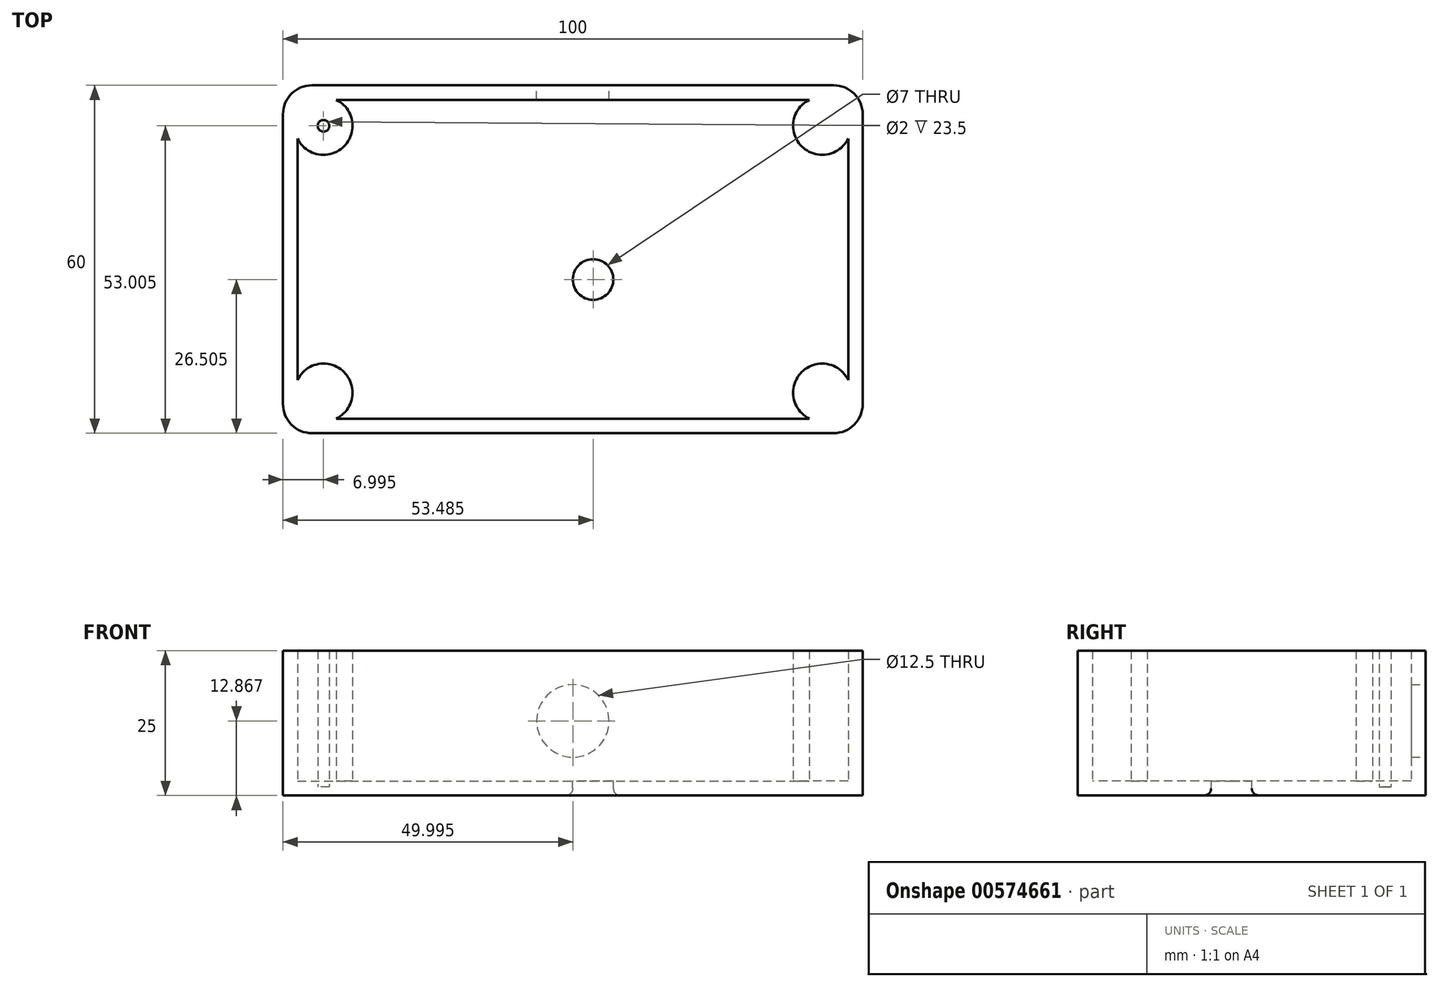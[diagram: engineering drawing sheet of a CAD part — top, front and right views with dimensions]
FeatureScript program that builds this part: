
annotation { "Feature Type Name" : "Feature", "Feature Type Description" : "" }
export const myFeature = defineFeature(function(context is Context, id is Id, definition is map)
    precondition{}
    {
        {
            var Q0;
            Q0=qCreatedBy(makeId("Top.planeOp"),FACE);
            var sketch = newSketch(context, id + "F0", { "sketchPlane" : qUnion([Q0])});
            skLineSegment(sketch, "E0.bottom", {"start": v(-26.94, 44.14) * mm, "end": v(73.06, 44.14) * mm});
            skLineSegment(sketch, "E0.top", {"start": v(-26.94, -15.86) * mm, "end": v(73.06, -15.86) * mm});
            skLineSegment(sketch, "E0.left", {"start": v(-26.94, 44.14) * mm, "end": v(-26.94, -15.86) * mm});
            skLineSegment(sketch, "E0.right", {"start": v(73.06, 44.14) * mm, "end": v(73.06, -15.86) * mm});
            skSolve(sketch);
        }
        {
            var Q0;
            Q0=makeQuery(id+"F0.imprint","IMPRINT",FACE,{"disambiguationData":[TD([[makeQuery(id+"F0.imprint","IMPRINT",EDGE,{"derivedFrom":sQuery(id+"F0.wireOp",EDGE,"E0.bottom")}),-1.0]])]});
            extrude(context, id + "F1", {"entities" : qUnion([Q0]), "depth" : 25 * mm, "offsetDistance" : 25 * mm});
        }
        {
            var Q0;
            Q0=makeQuery(id+"F1.opExtrude","CAP_FACE",FACE,{"disambiguationData":[OSD([sQuery(id+"F0.wireOp",EDGE,"E0.bottom"),sQuery(id+"F0.wireOp",EDGE,"E0.top"),sQuery(id+"F0.wireOp",EDGE,"E0.left"),sQuery(id+"F0.wireOp",EDGE,"E0.right")])],"isStart":false});
            shell(context, id + "F2", {"entities" : qUnion([Q0]), "thickness" : 2.5 * mm});
        }
        {
            var Q0;
            Q0=makeQuery(id+"F1.opExtrude","SWEPT_EDGE",EDGE,{"disambiguationData":[OSD([sQuery(id+"F0.wireOp",EDGE,"E0.bottom"),sQuery(id+"F0.wireOp",EDGE,"E0.left")])]});
            var Q1;
            Q1=makeQuery(id+"F1.opExtrude","SWEPT_EDGE",EDGE,{"disambiguationData":[OSD([sQuery(id+"F0.wireOp",EDGE,"E0.top"),sQuery(id+"F0.wireOp",EDGE,"E0.left")])]});
            var Q2;
            Q2=makeQuery(id+"F1.opExtrude","SWEPT_EDGE",EDGE,{"disambiguationData":[OSD([sQuery(id+"F0.wireOp",EDGE,"E0.top"),sQuery(id+"F0.wireOp",EDGE,"E0.right")])]});
            var Q3;
            Q3=makeQuery(id+"F1.opExtrude","SWEPT_EDGE",EDGE,{"disambiguationData":[OSD([sQuery(id+"F0.wireOp",EDGE,"E0.bottom"),sQuery(id+"F0.wireOp",EDGE,"E0.right")])]});
            fillet(context, id + "F3", {"entities" : qUnion([Q0, Q1, Q2, Q3]), "radius" : 5 * mm, "tangentPropagation" : true, "allowEdgeOverflow" : false});
        }
        {
            var Q0;
            Q0=makeQuery(id+"F2.opShell","OFFSET_EDGE",EDGE,{"disambiguationData":[OSD([sQuery(id+"F0.wireOp",EDGE,"E0.top"),sQuery(id+"F0.wireOp",EDGE,"E0.right")])]});
            var Q1;
            Q1=makeQuery(id+"F2.opShell","OFFSET_EDGE",EDGE,{"disambiguationData":[OSD([sQuery(id+"F0.wireOp",EDGE,"E0.bottom"),sQuery(id+"F0.wireOp",EDGE,"E0.left")])]});
            var Q2;
            Q2=makeQuery(id+"F2.opShell","OFFSET_EDGE",EDGE,{"disambiguationData":[OSD([sQuery(id+"F0.wireOp",EDGE,"E0.top"),sQuery(id+"F0.wireOp",EDGE,"E0.left")])]});
            var Q3;
            Q3=makeQuery(id+"F2.opShell","OFFSET_EDGE",EDGE,{"disambiguationData":[OSD([sQuery(id+"F0.wireOp",EDGE,"E0.bottom"),sQuery(id+"F0.wireOp",EDGE,"E0.right")])]});
            fillet(context, id + "F4", {"entities" : qUnion([Q0, Q1, Q2, Q3]), "radius" : 5 * mm, "tangentPropagation" : true, "allowEdgeOverflow" : false});
        }
        {
            var Q0;
            Q0=makeQuery(id+"F2.opShell","OFFSET_FACE",FACE,{"disambiguationData":[OSD([sQuery(id+"F0.wireOp",EDGE,"E0.bottom"),sQuery(id+"F0.wireOp",EDGE,"E0.top"),sQuery(id+"F0.wireOp",EDGE,"E0.left"),sQuery(id+"F0.wireOp",EDGE,"E0.right")])]});
            var sketch = newSketch(context, id + "F5", { "sketchPlane" : qUnion([Q0])});
            skCircle(sketch, "E1", {"center": v(26.55, 10.64) * mm, "radius": 3.5 * mm});
            skPoint(sketch, "E1.first.point", {"position": v(28.86, 13.27) * mm});
            skPoint(sketch, "E1.second.point", {"position": v(23.06, 10.9) * mm});
            skPoint(sketch, "E1.third.point", {"position": v(30.04, 10.77) * mm});
            skSolve(sketch);
        }
        {
            var Q0;
            Q0 = qSketchRegion(id + "F5", true);
            extrude(context, id + "F6", {"entities" : qUnion([Q0]), "operationType" : NewBodyOperationType.REMOVE, "oppositeDirection" : true, "depth" : 25 * mm, "offsetDistance" : 25 * mm});
        }
        {
            var Q0;
            Q0=makeQuery(id+"F6.boolean.opBoolean","INTERSECT",EDGE,{"derivedFrom":[makeQuery(id+"F1.opExtrude","CAP_FACE",FACE,{"disambiguationData":[OSD([sQuery(id+"F0.wireOp",EDGE,"E0.bottom"),sQuery(id+"F0.wireOp",EDGE,"E0.top"),sQuery(id+"F0.wireOp",EDGE,"E0.left"),sQuery(id+"F0.wireOp",EDGE,"E0.right")])],"isStart":true}),makeQuery(id+"F6.opExtrude","SWEPT_FACE",FACE,{"disambiguationData":[OSD([sQuery(id+"F5.wireOp",EDGE,"E1")])]})]});
            var Q1;
            Q1=makeQuery(id+"F6.boolean.opBoolean","COPY",EDGE,{"derivedFrom":makeQuery(id+"F6.opExtrude","CAP_EDGE",EDGE,{"disambiguationData":[OSD([sQuery(id+"F5.wireOp",EDGE,"E1")])],"isStart":true})});
            fillet(context, id + "F7", {"entities" : qUnion([Q0, Q1]), "radius" : 1.25 * mm, "tangentPropagation" : true, "allowEdgeOverflow" : false});
        }
        {
            var Q0;
            Q0=makeQuery(id+"F0.imprint","IMPRINT",FACE,{"disambiguationData":[TD([[makeQuery(id+"F0.imprint","IMPRINT",EDGE,{"derivedFrom":sQuery(id+"F0.wireOp",EDGE,"E0.bottom")}),-1.0]])]});
            var sketch = newSketch(context, id + "F8", { "sketchPlane" : qUnion([Q0])});
            skCircle(sketch, "E2", {"center": v(-19.94, 37.14) * mm, "radius": 5 * mm});
            skCircle(sketch, "E3", {"center": v(-19.94, 37.14) * mm, "radius": 1 * mm});
            skLineSegment(sketch, "E4", {"start": v(-27.15, -15.7) * mm, "end": v(73.34, -15.88) * mm, "construction": true});
            skSolve(sketch);
        }
        {
            var Q0;
            Q0 = qSketchRegion(id + "F8", true);
            extrude(context, id + "F9", {"entities" : qUnion([Q0]), "operationType" : NewBodyOperationType.ADD, "depth" : 25 * mm, "offsetDistance" : 25 * mm});
        }
        {
            var Q0;
            Q0=makeQuery(id+"F9.boolean.opBoolean","SPLIT",FACE,{"disambiguationData":[TD([makeQuery(id+"F9.opExtrude","SWEPT_FACE",FACE,{"disambiguationData":[OSD([sQuery(id+"F8.wireOp",EDGE,"E3")])]})])],"derivedFrom":makeQuery(id+"F2.opShell","OFFSET_FACE",FACE,{"disambiguationData":[OSD([sQuery(id+"F0.wireOp",EDGE,"E0.bottom"),sQuery(id+"F0.wireOp",EDGE,"E0.top"),sQuery(id+"F0.wireOp",EDGE,"E0.left"),sQuery(id+"F0.wireOp",EDGE,"E0.right")])]})});
            extrude(context, id + "F10", {"entities" : qUnion([Q0]), "operationType" : NewBodyOperationType.REMOVE, "oppositeDirection" : true, "depth" : 1 * mm, "offsetDistance" : 25 * mm, "hasSecondDirection" : true, "secondDirectionOppositeDirection" : false, "secondDirectionDepth" : 1 * mm});
        }
        {
            var Q0;
            Q0=makeQuery(id+"F0.imprint","IMPRINT",FACE,{"disambiguationData":[TD([[makeQuery(id+"F0.imprint","IMPRINT",EDGE,{"derivedFrom":sQuery(id+"F0.wireOp",EDGE,"E0.bottom")}),-1.0]])]});
            var sketch = newSketch(context, id + "F11", { "sketchPlane" : qUnion([Q0])});
            skCircle(sketch, "E5", {"center": v(66.06, 37.14) * mm, "radius": 5 * mm});
            skSolve(sketch);
        }
        {
            var Q0;
            Q0 = qSketchRegion(id + "F11", true);
            extrude(context, id + "F12", {"entities" : qUnion([Q0]), "operationType" : NewBodyOperationType.ADD, "depth" : 25 * mm, "offsetDistance" : 25 * mm});
        }
        {
            var Q0;
            Q0=makeQuery(id+"F0.imprint","IMPRINT",FACE,{"disambiguationData":[TD([[makeQuery(id+"F0.imprint","IMPRINT",EDGE,{"derivedFrom":sQuery(id+"F0.wireOp",EDGE,"E0.bottom")}),-1.0]])]});
            var sketch = newSketch(context, id + "F13", { "sketchPlane" : qUnion([Q0])});
            skCircle(sketch, "E6", {"center": v(-19.94, -8.86) * mm, "radius": 5 * mm});
            skSolve(sketch);
        }
        {
            var Q0;
            Q0 = qSketchRegion(id + "F13", true);
            extrude(context, id + "F14", {"entities" : qUnion([Q0]), "operationType" : NewBodyOperationType.ADD, "depth" : 25 * mm, "offsetDistance" : 25 * mm});
        }
        {
            var Q0;
            Q0=makeQuery(id+"F0.imprint","IMPRINT",FACE,{"disambiguationData":[TD([[makeQuery(id+"F0.imprint","IMPRINT",EDGE,{"derivedFrom":sQuery(id+"F0.wireOp",EDGE,"E0.bottom")}),-1.0]])]});
            var sketch = newSketch(context, id + "F15", { "sketchPlane" : qUnion([Q0])});
            skCircle(sketch, "E7", {"center": v(66.06, -8.86) * mm, "radius": 5 * mm});
            skSolve(sketch);
        }
        {
            var Q0;
            Q0 = qSketchRegion(id + "F15", true);
            extrude(context, id + "F16", {"entities" : qUnion([Q0]), "operationType" : NewBodyOperationType.ADD, "depth" : 25 * mm, "offsetDistance" : 25 * mm});
        }
        {
            var Q0;
            Q0=makeQuery(id+"F1.opExtrude","SWEPT_FACE",FACE,{"disambiguationData":[OSD([sQuery(id+"F0.wireOp",EDGE,"E0.bottom")])]});
            var sketch = newSketch(context, id + "F17", { "sketchPlane" : qUnion([Q0])});
            skCircle(sketch, "E8", {"center": v(-23.06, 12.87) * mm, "radius": 6.25 * mm});
            skSolve(sketch);
        }
        {
            var Q0;
            Q0 = qSketchRegion(id + "F17", true);
            extrude(context, id + "F18", {"entities" : qUnion([Q0]), "operationType" : NewBodyOperationType.REMOVE, "oppositeDirection" : true, "depth" : 10 * mm, "offsetDistance" : 25 * mm});
        }
    });
